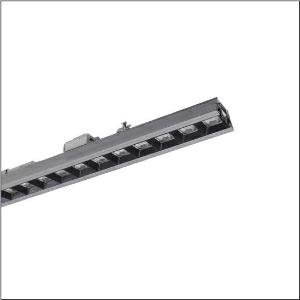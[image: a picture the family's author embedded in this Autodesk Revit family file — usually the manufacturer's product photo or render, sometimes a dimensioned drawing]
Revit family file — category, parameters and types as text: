
# Revit family: licross_r__21_silica_51ts12dn4zm00583xx_641b
name_source: partatom
category: Lighting Fixtures
units: mm (PartAtom-declared; Revit-internal decimal feet)

## family parameters
Cut with Voids When Loaded = No
Host = Face
Light Source = No
Part Type = Normal
Room Calculation Point = No
Round Connector Dimension = Use Diameter
Shared = No

## types (1)
- --- (1 x LED, 6340 lm, 39 W, 4000K)
    Apparent Load = 39 VA
    CIE Flux Codes = 86 100 100 100 100
    Color Rendering = 80
    Color Temperature = 4000K
    Default Elevation = 1800 mm
    Description = Licross® 21 Silica, luminaire insert, of sheet steel, galvanised, coil coated, silver, length: 1.500mm, width: 82mm, height: 86mm, LED rated luminous flux: 6.340lm, light colour: 840, control gear: DALI 2, with plug, 5-pole, with phase selection, mains connection: 220..240V, AC, 50/60Hz, rated input power: 39W, halogen-free wiring, primary light control with lens, of PMMA, primary anti-glare with darklight reflector, of PC, CAT 2 (L<= 1000cd/m²), light emission: direct distribution, primary light characteristic: symmetric, protection rating (complete): IP40, insulation class (complete): insulation class I (protective earthing), certification: CE, UKCA, protection symbol: D if used in an environment without relevant dust loads, impact resistance: IK03, permissible ambient temperature for indoor applications: -25..+45°C, corresponds to IFS (International Featured Standards) requirements for safety and quality in the food industry, reducing of maximum allowable ambient temperature of 5°C with ceiling mounting, LABS conformity tested according to VDMA 24364:2018-05, packaging unit: 1 piece
    Height = 86 mm
    Lamp = 1 x LED
    Lamp Light Flux = 6340 lm
    Lamp Power = 39 W
    Lamp count = 1
    Length = 1500 mm
    Luminous efficacy = 163 lm/W
    Manufacturer = Siteco
    ModVariant = No
    Model = 51TS12DN4ZM00583XX
    Mounting Place = Ceiling
    Mounting Type = Pendant
    Number of Poles = 1
    OnlyDefault = Yes
    Power Factor = 1
    Product Name = Licross® 21 Silica
    Product group = luminaire insert
    ProductGroupID = 901
    Protection Class = Protection class I
    Protection Degree = IP 40
    RLX_Detail_Level = 1
    RLX_Emergency_Light_Flux = 0 lm
    RLX_Emergency_Type = 0
    RLX_Emergency_Type_DB = No
    RlxData = <blob elided: 56989 chars, md5=3493f156>
    Socket = socket
    Standby Power = 0 W
    System Light Flux = 6340 lm
    System Power = 39 W
    Type Comments = factory setting: luminous flux: 100 % | dim-lin: 254 | 435 mA
    Type Image = l_1290833.jpg
    URL = http://relux.com
    VarID = @adj_054679
    Voltage = 0 V
    Weight = 0.00 kg
    Width = 82 mm  [stored 0.269029 ft]

note: [stored X ft] marks values corroborated as IEEE doubles in the binary element streams (Revit-internal decimal feet)

## geometry (parser evidence)
native form markers: Blend x4, Sweep x11
no freeform markers — native parametric forms only
